# Revit family: Triple_Bowl_Drop-in_Sink-Elkay-LTR5422101_6
name_source: partatom
category: Plumbing Fixtures
units: mm (PartAtom-declared; Revit-internal decimal feet)

## family parameters
Cut with Voids When Loaded = No
Host = Face
Maintain Annotation Orientation = No
OmniClass Number = 23.45.05.14.14
OmniClass Title = Sinks/Lavatories
Part Type = Normal
Room Calculation Point = No
Round Connector Dimension = Use Diameter
Shared = No

## types (5) — shared parameters
Approx. Shipping Weight (lbs) = 60
Assembly Code = D2010410
Back Flange = 4.25 "
Bowl  Dimensions 1 = 16 inch x 16 inch x 10 inch
Bowl  Dimensions 2 = 16 inch x 16 inch x 10 inch
Bowl  Dimensions 3 = 16 inch x 16 inch x 10 inch
Bowl Depth = 10 "
Bowl Length 1 = 16 "
Bowl Length 2 = 16 "
Bowl Length 3 = 16 "
Bowl Width = 16 "
CL of Faucet Hole = 2.25 "
Cutting Length = 53.375 "
Cutting Width = 21.375 "
Darin and Pitch height = 0.65 "
Default Elevation = 48 "
Description = Lustertone® Classic Stainless Steel 54 inch x 22 inch x 10 1/8 inch Triple Bowl Drop-in Sink
Drain Location = Center
Drain Location Along X- Axis = 8 "
Drain Location Along Y- Axis = 8 "
Drain Size = 3.5 "
Front Flange = 1.75 "
Gauge = 18
Installation Type = Drop-in
Left Flange = 1.75 "
Length of Sink = 54 "
Main Material = Finish-Elkay-Stainless Steel
Manufacturer = Elkay Manufacturer Company
Manufacturer Brand = Elkay (by Zurn Elkay Water Solutions)
Masking Region for Bowl = 1.75 "
Number of Bowls = 3
Outlet Connection Size (inch) = 1.5 "
Overall Bowl Length = 50.5 "
Product Documentation Link = https://www.elkayfiles.com
Product Installation Sheet URL = https://www.elkayfiles.com
Product Page URL = https://www.elkay.com
Product Weight (lbs) = 50
Product data URL = https://www.bimobject.com
R1 for Rim = 0.09 "
R2 for Rim = 0.06 "
Radius for Bowl = 1.76 "
Radius for cutting endge = 1.5 "
Repair Parts URL = https://www.elkayfiles.com
Right Flange = 1.75 "
Rim Height = 0.125 "
Sink Depth = 10.125 "
Sink Dimensions = 54 inch x 22 inch x 10 1/8 inch
U-channel Length along -X axis = 49 "
U-channel Length along -Y axis = 17 "
URL = https://www.elkay.com
Vertical Radius = 1.75 "
Width of Sink = 22 "

## per-type parameters (varying)
| type | Hole 2 | Hole- 6 | Hole-1 | Hole-2 | Hole-3 | Hole-4 | Hole-5 | Model | center to center distance between 3rd and 4th hole |
| LTR5422101 (Triple Bowl Drop-in Sink) | 25.25 " | No | No | Yes | No | No | No | LTR5422101 | 25.25 " |
| LTR5422102 (Triple Bowl Drop-in Sink) | 25.25 " | No | No | No | Yes | Yes | No | LTR5422102 | 17.25 " |
| LTR5422103 (Triple Bowl Drop-in Sink) | 25.25 " | No | No | Yes | Yes | Yes | No | LTR5422103 | 8 " |
| LTR5422106 (Triple Bowl Drop-in Sink) | 16.625 " | Yes | Yes | Yes | Yes | Yes | Yes | LTR5422106 | 9.25 " |
| LTR5422104 (Triple Bowl Drop-in Sink) | 25.25 " | No | No | Yes | Yes | Yes | Yes | LTR5422104 | 8 " |

## geometry (parser evidence)
native form markers: Sweep x3
no freeform markers — native parametric forms only
